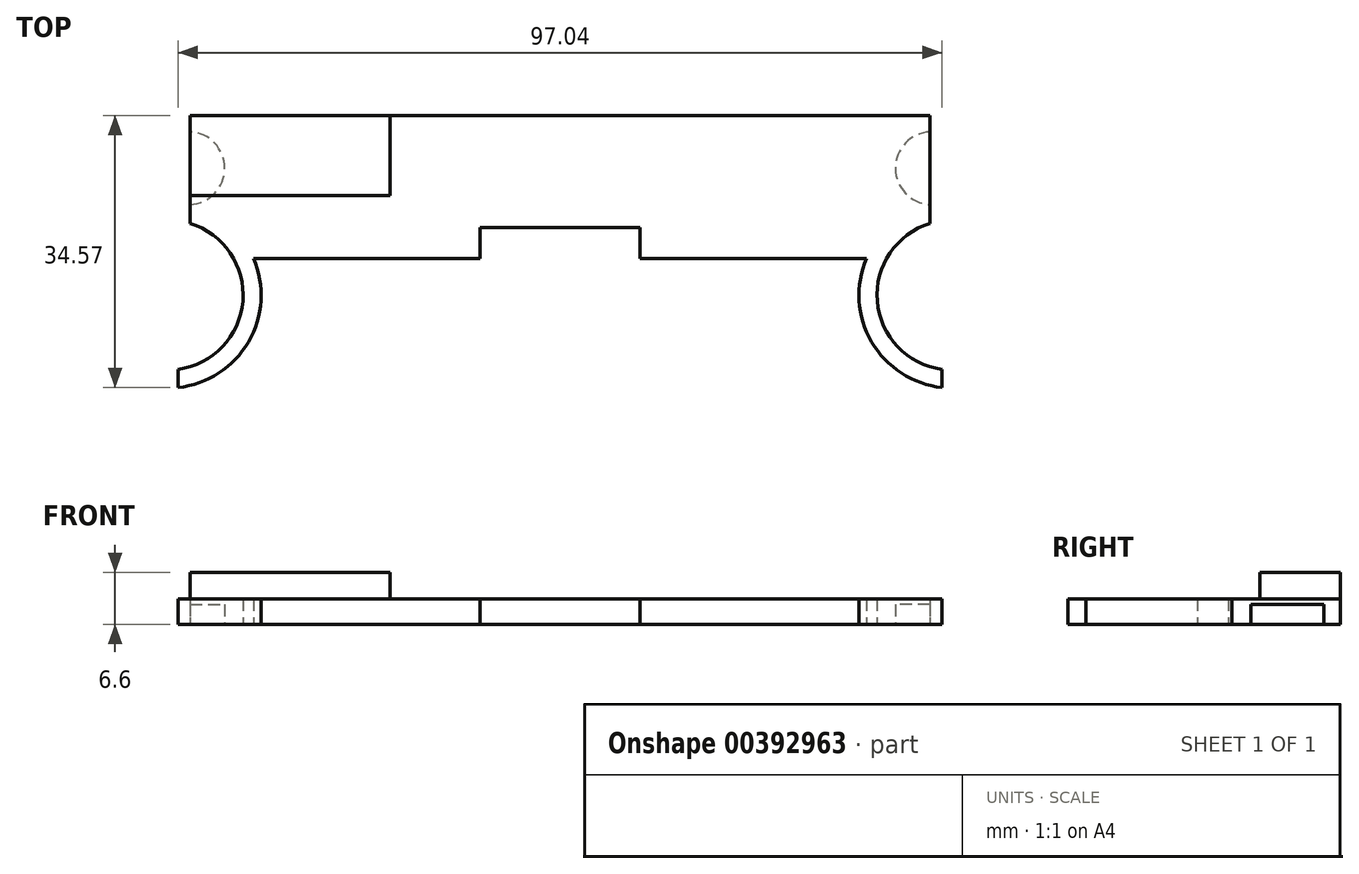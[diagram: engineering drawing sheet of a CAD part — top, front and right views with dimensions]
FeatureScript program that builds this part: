
annotation { "Feature Type Name" : "Feature", "Feature Type Description" : "" }
export const myFeature = defineFeature(function(context is Context, id is Id, definition is map)
    precondition{}
    {
        {
            var Q0;
            Q0=qCreatedBy(makeId("Top.planeOp"),FACE);
            var sketch = newSketch(context, id + "F0", { "sketchPlane" : qUnion([Q0])});
            skLineSegment(sketch, "E0.bottom", {"start": v(-47, 18.16) * mm, "end": v(47, 18.16) * mm});
            skLineSegment(sketch, "E0.top", {"start": v(-38.93, 0) * mm, "end": v(-10.16, 0) * mm});
            skLineSegment(sketch, "E0.left", {"start": v(-47, 18.16) * mm, "end": v(-47, 4.44) * mm});
            skLineSegment(sketch, "E0.right", {"start": v(47, 18.16) * mm, "end": v(47, 4.44) * mm});
            skArc(sketch, "E1", {"start": v(-49.78, -14.19) * mm, "mid": v(-40.36, -6.08) * mm, "end": v(-47, 4.44) * mm});
            skArc(sketch, "E2", {"start": v(-49.78, -16.48) * mm, "mid": v(-39.92, -11.16) * mm, "end": v(-38.93, 0) * mm});
            skLineSegment(sketch, "E3", {"start": v(-49.78, -14.19) * mm, "end": v(-49.78, -16.48) * mm});
            skArc(sketch, "E4.MirrorCS", {"start": v(49.78, -16.48) * mm, "mid": v(39.92, -11.16) * mm, "end": v(38.93, 0) * mm});
            skArc(sketch, "E5.MirrorCS", {"start": v(49.78, -14.19) * mm, "mid": v(40.36, -6.08) * mm, "end": v(47, 4.44) * mm});
            skLineSegment(sketch, "E6.MirrorCS", {"start": v(49.78, -14.19) * mm, "end": v(49.78, -16.48) * mm});
            skPoint(sketch, "E7.orphan", {"position": v(47, 0) * mm});
            skLineSegment(sketch, "E8.bottom", {"start": v(10.16, 3.94) * mm, "end": v(-10.16, 3.94) * mm});
            skLineSegment(sketch, "E8.left", {"start": v(10.16, 3.94) * mm, "end": v(10.16, 0) * mm});
            skLineSegment(sketch, "E8.right", {"start": v(-10.16, 3.94) * mm, "end": v(-10.16, 0) * mm});
            skPoint(sketch, "E8.middle", {"position": v(0, 0) * mm});
            skPoint(sketch, "E9.orphan", {"position": v(10.16, -3.94) * mm});
            skPoint(sketch, "E10.orphan", {"position": v(-10.16, -3.94) * mm});
            skLineSegment(sketch, "E11.trimOffspring", {"start": v(10.16, 0) * mm, "end": v(38.93, 0) * mm});
            skSolve(sketch);
        }
        {
            var Q0;
            Q0=qSketchRegion(id+"F0",true);
            extrude(context, id + "F1", {"entities" : qUnion([Q0]), "depth" : 3.23 * mm, "offsetDistance" : 25.4 * mm});
        }
        {
            var Q0;
            Q0=makeQuery(id+"F1.opExtrude","CAP_FACE",FACE,{"disambiguationData":[OSD([sQuery(id+"F0.wireOp",EDGE,"E0.bottom"),sQuery(id+"F0.wireOp",EDGE,"E0.top"),sQuery(id+"F0.wireOp",EDGE,"E0.left"),sQuery(id+"F0.wireOp",EDGE,"E0.right"),sQuery(id+"F0.wireOp",EDGE,"E1"),sQuery(id+"F0.wireOp",EDGE,"E2"),sQuery(id+"F0.wireOp",EDGE,"E3"),sQuery(id+"F0.wireOp",EDGE,"E4.MirrorCS"),sQuery(id+"F0.wireOp",EDGE,"E5.MirrorCS"),sQuery(id+"F0.wireOp",EDGE,"E6.MirrorCS"),sQuery(id+"F0.wireOp",EDGE,"BNhSm9uN-eiEH-wQ1g-g6A0-KiHbVTDSFtF1.top"),sQuery(id+"F0.wireOp",EDGE,"BNhSm9uN-eiEH-wQ1g-g6A0-KiHbVTDSFtF1.left"),sQuery(id+"F0.wireOp",EDGE,"BNhSm9uN-eiEH-wQ1g-g6A0-KiHbVTDSFtF1.right"),sQuery(id+"F0.wireOp",EDGE,"bccd14c4-18d1-4b62-ba9d-f6f005a7e31e.trimOffspring")])],"isStart":false});
            var sketch = newSketch(context, id + "F2", { "sketchPlane" : qUnion([Q0])});
            skLineSegment(sketch, "E12.bottom", {"start": v(-47, 8) * mm, "end": v(-21.59, 8) * mm});
            skLineSegment(sketch, "E12.top", {"start": v(-47, 18.16) * mm, "end": v(-21.59, 18.16) * mm});
            skLineSegment(sketch, "E12.left", {"start": v(-47, 8) * mm, "end": v(-47, 18.16) * mm});
            skLineSegment(sketch, "E12.right", {"start": v(-21.59, 8) * mm, "end": v(-21.59, 18.16) * mm});
            skSolve(sketch);
        }
        {
            var Q0;
            Q0=qSketchRegion(id+"F2",true);
            extrude(context, id + "F3", {"entities" : qUnion([Q0]), "operationType" : NewBodyOperationType.ADD, "depth" : 3.38 * mm});
        }
        {
            var Q0;
            Q0=makeQuery(id+"F1.opExtrude","CAP_FACE",FACE,{"disambiguationData":[OSD([sQuery(id+"F0.wireOp",EDGE,"E0.bottom"),sQuery(id+"F0.wireOp",EDGE,"E0.top"),sQuery(id+"F0.wireOp",EDGE,"E0.left"),sQuery(id+"F0.wireOp",EDGE,"E0.right"),sQuery(id+"F0.wireOp",EDGE,"E1"),sQuery(id+"F0.wireOp",EDGE,"E2"),sQuery(id+"F0.wireOp",EDGE,"E3"),sQuery(id+"F0.wireOp",EDGE,"E4.MirrorCS"),sQuery(id+"F0.wireOp",EDGE,"E5.MirrorCS"),sQuery(id+"F0.wireOp",EDGE,"E6.MirrorCS"),sQuery(id+"F0.wireOp",EDGE,"E8.bottom"),sQuery(id+"F0.wireOp",EDGE,"E8.left"),sQuery(id+"F0.wireOp",EDGE,"E8.right"),sQuery(id+"F0.wireOp",EDGE,"E11.trimOffspring")])],"isStart":true});
            var sketch = newSketch(context, id + "F4", { "sketchPlane" : qUnion([Q0])});
            skArc(sketch, "E13", {"start": v(-47, -16.08) * mm, "mid": v(-42.6, -11.45) * mm, "end": v(-47, -6.82) * mm});
            skArc(sketch, "E14.MirrorCS", {"start": v(47, -16.08) * mm, "mid": v(42.6, -11.45) * mm, "end": v(47, -6.82) * mm});
            skLineSegment(sketch, "E15", {"start": v(-47, -6.82) * mm, "end": v(-47, -16.08) * mm});
            skLineSegment(sketch, "E16.MirrorCS", {"start": v(47, -6.82) * mm, "end": v(47, -16.08) * mm});
            skSolve(sketch);
        }
        {
            var Q0;
            Q0 = qSketchRegion(id + "F4", true);
            extrude(context, id + "F5", {"entities" : qUnion([Q0]), "operationType" : NewBodyOperationType.REMOVE, "oppositeDirection" : true, "depth" : 2.54 * mm, "offsetDistance" : 25.4 * mm});
        }
        {
            var Q0;
            Q0=makeQuery(id+"F1.opExtrude","CAP_FACE",FACE,{"disambiguationData":[OSD([sQuery(id+"F0.wireOp",EDGE,"E0.bottom"),sQuery(id+"F0.wireOp",EDGE,"E0.top"),sQuery(id+"F0.wireOp",EDGE,"E0.left"),sQuery(id+"F0.wireOp",EDGE,"E0.right"),sQuery(id+"F0.wireOp",EDGE,"E1"),sQuery(id+"F0.wireOp",EDGE,"E2"),sQuery(id+"F0.wireOp",EDGE,"E3"),sQuery(id+"F0.wireOp",EDGE,"E4.MirrorCS"),sQuery(id+"F0.wireOp",EDGE,"E5.MirrorCS"),sQuery(id+"F0.wireOp",EDGE,"E6.MirrorCS"),sQuery(id+"F0.wireOp",EDGE,"E8.bottom"),sQuery(id+"F0.wireOp",EDGE,"E8.left"),sQuery(id+"F0.wireOp",EDGE,"E8.right"),sQuery(id+"F0.wireOp",EDGE,"E11.trimOffspring")])],"isStart":false});
            var sketch = newSketch(context, id + "F6", { "sketchPlane" : qUnion([Q0])});
            skLineSegment(sketch, "E17", {"start": v(-48.52, -14.1) * mm, "end": v(-48.52, -16.4) * mm});
            skArc(sketch, "E18.0", {"start": v(-49.78, -14.19) * mm, "mid": v(-49.15, -14.17) * mm, "end": v(-48.52, -14.1) * mm});
            skLineSegment(sketch, "E18.1", {"start": v(-49.78, -14.19) * mm, "end": v(-49.78, -16.48) * mm});
            skArc(sketch, "E18.2", {"start": v(-49.78, -16.48) * mm, "mid": v(-49.15, -16.46) * mm, "end": v(-48.52, -16.4) * mm});
            skPoint(sketch, "E19.orphan", {"position": v(-47, 4.44) * mm});
            skPoint(sketch, "E20.orphan", {"position": v(-38.93, 0) * mm});
            skArc(sketch, "E21.MirrorCS", {"start": v(49.78, -16.48) * mm, "mid": v(49.15, -16.46) * mm, "end": v(48.52, -16.4) * mm});
            skLineSegment(sketch, "E22.MirrorCS", {"start": v(49.78, -14.19) * mm, "end": v(49.78, -16.48) * mm});
            skArc(sketch, "E23.MirrorCS", {"start": v(49.78, -14.19) * mm, "mid": v(49.15, -14.17) * mm, "end": v(48.52, -14.1) * mm});
            skLineSegment(sketch, "E24.MirrorCS", {"start": v(48.52, -14.1) * mm, "end": v(48.52, -16.4) * mm});
            skSolve(sketch);
        }
        {
            var Q0;
            Q0 = qSketchRegion(id + "F6", true);
            extrude(context, id + "F7", {"entities" : qUnion([Q0]), "operationType" : NewBodyOperationType.REMOVE, "endBound" : BoundingType.THROUGH_ALL, "oppositeDirection" : true, "depth" : 25.4 * mm, "offsetDistance" : 25.4 * mm});
        }
    });
